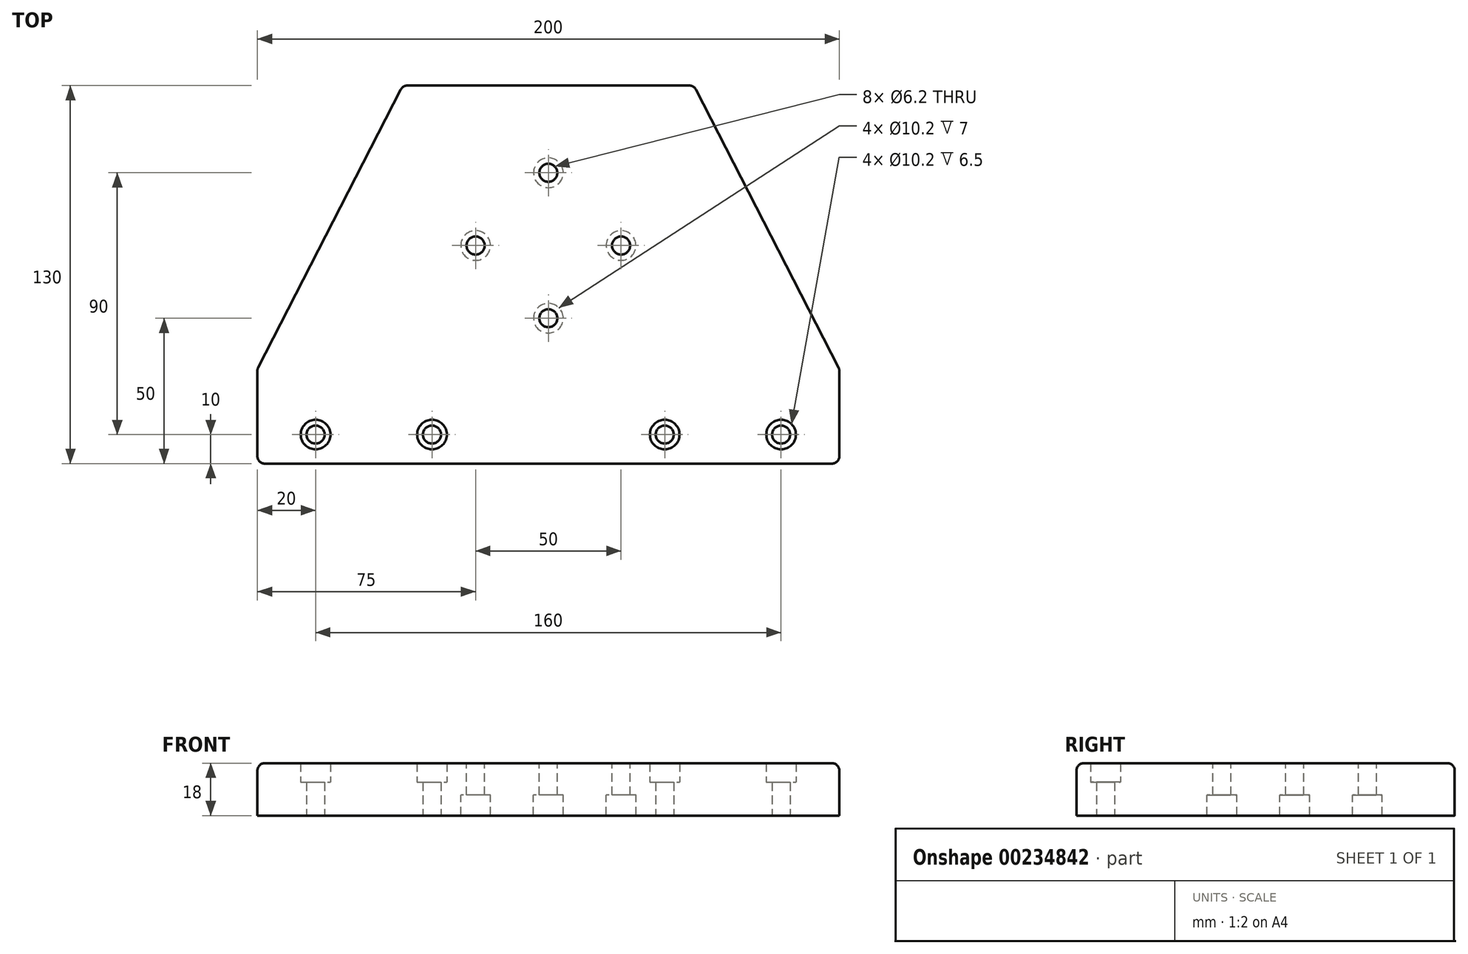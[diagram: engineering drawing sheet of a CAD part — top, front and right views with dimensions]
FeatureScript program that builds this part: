
annotation { "Feature Type Name" : "Feature", "Feature Type Description" : "" }
export const myFeature = defineFeature(function(context is Context, id is Id, definition is map)
    precondition{}
    {
        {
            var Q0;
            Q0=qCreatedBy(makeId("Top.planeOp"),FACE);
            var sketch = newSketch(context, id + "F0", { "sketchPlane" : qUnion([Q0])});
            skLineSegment(sketch, "E0", {"start": v(0, 0) * mm, "end": v(-100, 0) * mm});
            skLineSegment(sketch, "E1", {"start": v(-100, 0) * mm, "end": v(-100, 130) * mm});
            skLineSegment(sketch, "E2", {"start": v(-100, 130) * mm, "end": v(0, 130) * mm});
            skLineSegment(sketch, "E3", {"start": v(0, 130) * mm, "end": v(0, 109.88) * mm});
            skLineSegment(sketch, "E4.MirrorCS", {"start": v(100, 130) * mm, "end": v(0, 130) * mm});
            skLineSegment(sketch, "E5.MirrorCS", {"start": v(100, 0) * mm, "end": v(100, 130) * mm});
            skLineSegment(sketch, "E6.MirrorCS", {"start": v(0, 0) * mm, "end": v(100, 0) * mm});
            skLineSegment(sketch, "E7", {"start": v(-100, 0) * mm, "end": v(-80, 0) * mm});
            skLineSegment(sketch, "E8", {"start": v(-80, 0) * mm, "end": v(-80, 10) * mm});
            skLineSegment(sketch, "E9", {"start": v(-80, 10) * mm, "end": v(-40, 10) * mm});
            skLineSegment(sketch, "E10.MirrorCS", {"start": v(80, 10) * mm, "end": v(40, 10) * mm});
            skLineSegment(sketch, "E11", {"start": v(0, 0) * mm, "end": v(0, 75) * mm});
            skLineSegment(sketch, "E12", {"start": v(0, 75) * mm, "end": v(-25, 75) * mm});
            skLineSegment(sketch, "E13", {"start": v(0, 75) * mm, "end": v(0, 50) * mm});
            skLineSegment(sketch, "E14", {"start": v(0, 75) * mm, "end": v(0, 100) * mm});
            skLineSegment(sketch, "E15.MirrorCS", {"start": v(0, 75) * mm, "end": v(25, 75) * mm});
            skLineSegment(sketch, "E16", {"start": v(-100, 65) * mm, "end": v(-50, 130) * mm});
            skLineSegment(sketch, "E17", {"start": v(50, 130) * mm, "end": v(100, 65) * mm});
            skLineSegment(sketch, "E18", {"start": v(-100, 0) * mm, "end": v(-100, 65) * mm});
            skLineSegment(sketch, "E19", {"start": v(-100, 32.5) * mm, "end": v(-50, 130) * mm});
            skLineSegment(sketch, "E20", {"start": v(100, 0) * mm, "end": v(100, 65) * mm});
            skLineSegment(sketch, "E21", {"start": v(100, 32.5) * mm, "end": v(50, 130) * mm});
            skSolve(sketch);
        }
        {
            var Q0;
            Q0=makeQuery(id+"F0.imprint","IMPRINT",FACE,{"disambiguationData":[TD([[makeQuery(id+"F0.imprint","IMPRINT",EDGE,{"derivedFrom":sQuery(id+"F0.wireOp",EDGE,"E0")}),-1.0]])]});
            extrude(context, id + "F1", {"entities" : qUnion([Q0]), "depth" : 18 * mm});
        }
        {
            var Q0;
            Q0=sQuery(id+"F0.wireOp",VERTEX,"E14.end");
            var Q1;
            Q1=sQuery(id+"F0.wireOp",VERTEX,"E15.MirrorCS.end");
            var Q2;
            Q2=sQuery(id+"F0.wireOp",VERTEX,"E13.end");
            var Q3;
            Q3=sQuery(id+"F0.wireOp",VERTEX,"E12.end");
            var Q4;
            Q4=makeQuery(id+"F1.opExtrude","SWEPT_BODY",BODY,{"disambiguationData":[OSD([sQuery(id+"F0.wireOp",EDGE,"E0"),sQuery(id+"F0.wireOp",EDGE,"E1"),sQuery(id+"F0.wireOp",EDGE,"E2"),sQuery(id+"F0.wireOp",EDGE,"E4.MirrorCS"),sQuery(id+"F0.wireOp",EDGE,"E5.MirrorCS"),sQuery(id+"F0.wireOp",EDGE,"E6.MirrorCS"),sQuery(id+"F0.wireOp",EDGE,"E7")])]});
            hole(context, id + "F2", {"style" : HoleStyle.C_BORE, "endStyle" : HoleEndStyle.THROUGH, "oppositeDirection" : true, "holeDiameter" : 6.2 * mm, "cBoreDiameter" : 10.2 * mm, "cBoreDepth" : 7 * mm, "locations" : qUnion([Q0, Q1, Q2, Q3]), "scope" : qUnion([Q4]), "isTappedThrough" : true, "startStyle" : HoleStartStyle.PART});
        }
        {
            var Q0;
            Q0=makeQuery(id+"F1.opExtrude","CAP_FACE",FACE,{"disambiguationData":[OSD([sQuery(id+"F0.wireOp",EDGE,"E0"),sQuery(id+"F0.wireOp",EDGE,"E1"),sQuery(id+"F0.wireOp",EDGE,"E2"),sQuery(id+"F0.wireOp",EDGE,"E4.MirrorCS"),sQuery(id+"F0.wireOp",EDGE,"E5.MirrorCS"),sQuery(id+"F0.wireOp",EDGE,"E6.MirrorCS"),sQuery(id+"F0.wireOp",EDGE,"E7")])],"isStart":false});
            var sketch = newSketch(context, id + "F3", { "sketchPlane" : qUnion([Q0])});
            skLineSegment(sketch, "E22", {"start": v(-100, 0) * mm, "end": v(-80, 0) * mm});
            skLineSegment(sketch, "E23", {"start": v(-80, 0) * mm, "end": v(-80, 10) * mm});
            skLineSegment(sketch, "E24", {"start": v(-80, 10) * mm, "end": v(-40, 10) * mm});
            skLineSegment(sketch, "E25", {"start": v(0, 0) * mm, "end": v(0, 11.71) * mm});
            skLineSegment(sketch, "E26.MirrorCS", {"start": v(80, 10) * mm, "end": v(40, 10) * mm});
            skSolve(sketch);
        }
        {
            var Q0;
            Q0=sQuery(id+"F3.wireOp",VERTEX,"E24.start");
            var Q1;
            Q1=sQuery(id+"F3.wireOp",VERTEX,"E24.end");
            var Q2;
            Q2=sQuery(id+"F3.wireOp",VERTEX,"E26.MirrorCS.end");
            var Q3;
            Q3=sQuery(id+"F3.wireOp",VERTEX,"E26.MirrorCS.start");
            var Q4;
            Q4=makeQuery(id+"F1.opExtrude","SWEPT_BODY",BODY,{"disambiguationData":[OSD([sQuery(id+"F0.wireOp",EDGE,"E0"),sQuery(id+"F0.wireOp",EDGE,"E1"),sQuery(id+"F0.wireOp",EDGE,"E2"),sQuery(id+"F0.wireOp",EDGE,"E4.MirrorCS"),sQuery(id+"F0.wireOp",EDGE,"E5.MirrorCS"),sQuery(id+"F0.wireOp",EDGE,"E6.MirrorCS"),sQuery(id+"F0.wireOp",EDGE,"E7")])]});
            hole(context, id + "F4", {"style" : HoleStyle.C_BORE, "endStyle" : HoleEndStyle.THROUGH, "holeDiameter" : 6.2 * mm, "cBoreDiameter" : 10.2 * mm, "cBoreDepth" : 6.5 * mm, "locations" : qUnion([Q0, Q1, Q2, Q3]), "scope" : qUnion([Q4]), "isTappedThrough" : true, "startStyle" : HoleStartStyle.PART});
        }
        {
            var Q0;
            Q0=makeQuery(id+"F1.opExtrude","SWEPT_EDGE",EDGE,{"disambiguationData":[OSD([sQuery(id+"F0.wireOp",EDGE,"E1"),sQuery(id+"F0.wireOp",EDGE,"E16")])]});
            var Q1;
            Q1=makeQuery(id+"F1.opExtrude","SWEPT_EDGE",EDGE,{"disambiguationData":[OSD([sQuery(id+"F0.wireOp",EDGE,"E5.MirrorCS"),sQuery(id+"F0.wireOp",EDGE,"E17")])]});
            var Q2;
            Q2=makeQuery(id+"F1.opExtrude","CAP_EDGE",EDGE,{"disambiguationData":[OSD([sQuery(id+"F0.wireOp",EDGE,"E1")])],"isStart":false});
            var Q3;
            Q3=makeQuery(id+"F1.opExtrude","CAP_EDGE",EDGE,{"disambiguationData":[OSD([sQuery(id+"F0.wireOp",EDGE,"E0"),sQuery(id+"F0.wireOp",EDGE,"E6.MirrorCS"),sQuery(id+"F0.wireOp",EDGE,"E7")])],"isStart":false});
            var Q4;
            Q4=makeQuery(id+"F1.opExtrude","CAP_EDGE",EDGE,{"disambiguationData":[OSD([sQuery(id+"F0.wireOp",EDGE,"E5.MirrorCS")])],"isStart":false});
            var Q5;
            Q5=makeQuery(id+"F1.opExtrude","CAP_EDGE",EDGE,{"disambiguationData":[OSD([sQuery(id+"F0.wireOp",EDGE,"E17")])],"isStart":false});
            var Q6;
            Q6=makeQuery(id+"F1.opExtrude","CAP_EDGE",EDGE,{"disambiguationData":[OSD([sQuery(id+"F0.wireOp",EDGE,"E2"),sQuery(id+"F0.wireOp",EDGE,"E4.MirrorCS")])],"isStart":false});
            var Q7;
            Q7=makeQuery(id+"F1.opExtrude","CAP_EDGE",EDGE,{"disambiguationData":[OSD([sQuery(id+"F0.wireOp",EDGE,"E16")])],"isStart":false});
            var Q8;
            Q8=makeQuery(id+"F1.opExtrude","SWEPT_EDGE",EDGE,{"disambiguationData":[OSD([sQuery(id+"F0.wireOp",EDGE,"E4.MirrorCS"),sQuery(id+"F0.wireOp",EDGE,"E17")])]});
            var Q9;
            Q9=makeQuery(id+"F1.opExtrude","SWEPT_EDGE",EDGE,{"disambiguationData":[OSD([sQuery(id+"F0.wireOp",EDGE,"E2"),sQuery(id+"F0.wireOp",EDGE,"E16")])]});
            var Q10;
            Q10=makeQuery(id+"F1.opExtrude","SWEPT_EDGE",EDGE,{"disambiguationData":[OSD([sQuery(id+"F0.wireOp",EDGE,"E5.MirrorCS"),sQuery(id+"F0.wireOp",EDGE,"E6.MirrorCS")])]});
            var Q11;
            Q11=makeQuery(id+"F1.opExtrude","SWEPT_EDGE",EDGE,{"disambiguationData":[OSD([sQuery(id+"F0.wireOp",EDGE,"E1"),sQuery(id+"F0.wireOp",EDGE,"E7")])]});
            var Q12;
            Q12=makeQuery(id+"F1.opExtrude","CAP_EDGE",EDGE,{"disambiguationData":[OSD([sQuery(id+"F0.wireOp",EDGE,"E19")])],"isStart":false});
            var Q13;
            Q13=makeQuery(id+"F1.opExtrude","SWEPT_EDGE",EDGE,{"disambiguationData":[OSD([sQuery(id+"F0.wireOp",EDGE,"E18"),sQuery(id+"F0.wireOp",EDGE,"E19")])]});
            var Q14;
            Q14=makeQuery(id+"F1.opExtrude","SWEPT_EDGE",EDGE,{"disambiguationData":[OSD([sQuery(id+"F0.wireOp",EDGE,"E20"),sQuery(id+"F0.wireOp",EDGE,"E21")])]});
            var Q15;
            Q15=makeQuery(id+"F1.opExtrude","CAP_EDGE",EDGE,{"disambiguationData":[OSD([sQuery(id+"F0.wireOp",EDGE,"E21")])],"isStart":false});
            var Q16;
            Q16=makeQuery(id+"F1.opExtrude","CAP_EDGE",EDGE,{"disambiguationData":[OSD([sQuery(id+"F0.wireOp",EDGE,"E20")])],"isStart":false});
            var Q17;
            Q17=makeQuery(id+"F1.opExtrude","CAP_EDGE",EDGE,{"disambiguationData":[OSD([sQuery(id+"F0.wireOp",EDGE,"E18")])],"isStart":false});
            fillet(context, id + "F5", {"entities" : qUnion([Q0, Q1, Q2, Q3, Q4, Q5, Q6, Q7, Q8, Q9, Q10, Q11, Q12, Q13, Q14, Q15, Q16, Q17]), "radius" : 2.5 * mm, "tangentPropagation" : true, "allowEdgeOverflow" : false});
        }
    });
